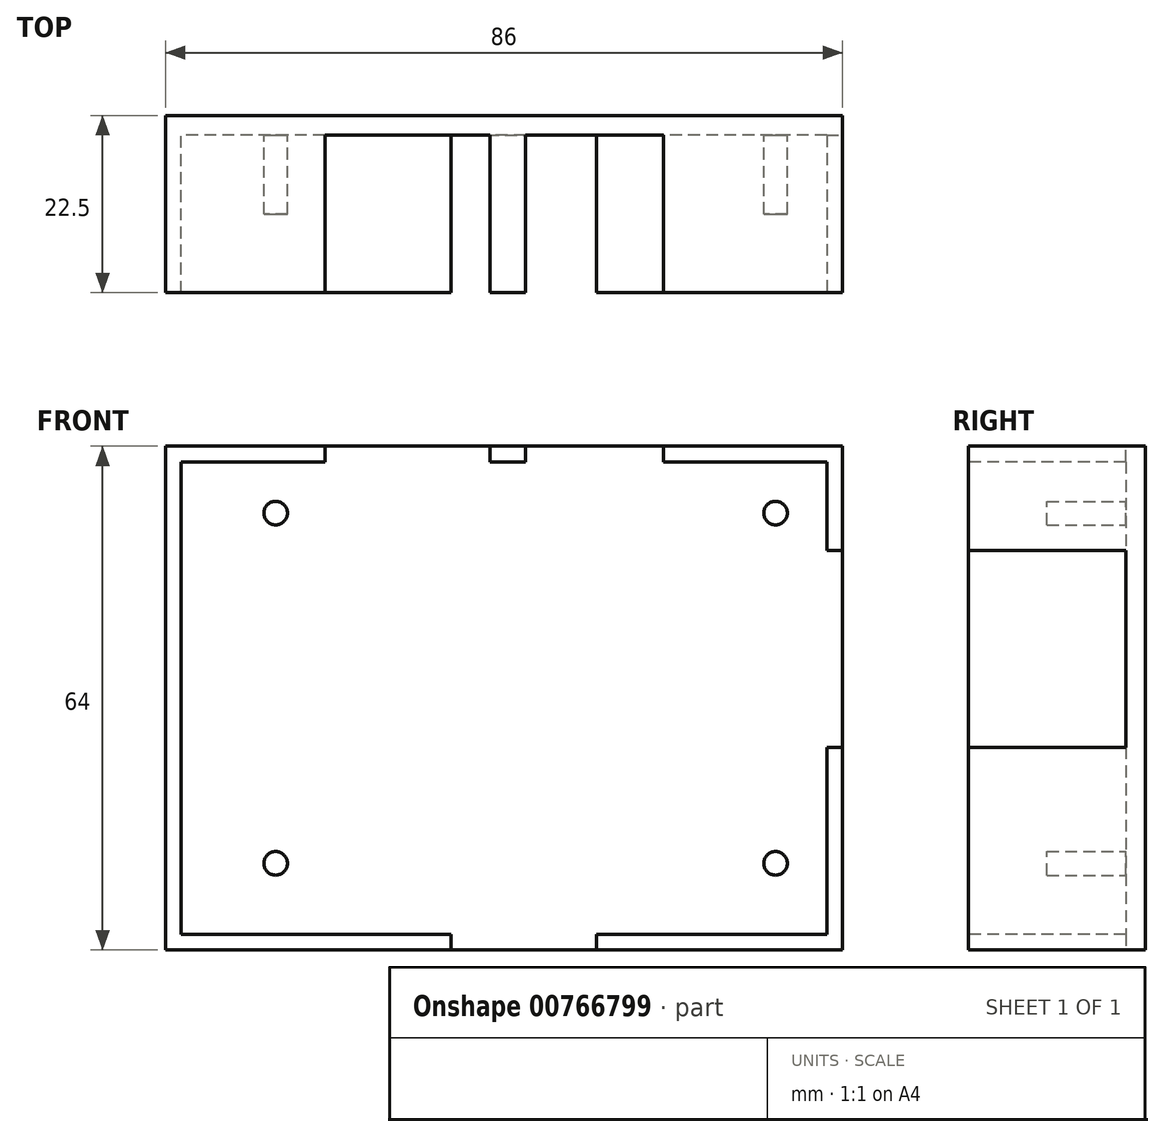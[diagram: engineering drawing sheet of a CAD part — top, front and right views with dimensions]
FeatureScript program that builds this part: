
annotation { "Feature Type Name" : "Feature", "Feature Type Description" : "" }
export const myFeature = defineFeature(function(context is Context, id is Id, definition is map)
    precondition{}
    {
        {
            var Q0;
            Q0=qCreatedBy(makeId("Front.planeOp"),FACE);
            var sketch = newSketch(context, id + "F0", { "sketchPlane" : qUnion([Q0])});
            skLineSegment(sketch, "E0.bottom", {"start": v(41, 30) * mm, "end": v(-41, 30) * mm});
            skLineSegment(sketch, "E0.top", {"start": v(41, -30) * mm, "end": v(-41, -30) * mm});
            skLineSegment(sketch, "E0.left", {"start": v(41, 30) * mm, "end": v(41, -30) * mm});
            skLineSegment(sketch, "E0.right", {"start": v(-41, 30) * mm, "end": v(-41, -30) * mm});
            skPoint(sketch, "E0.middle", {"position": v(0, 0) * mm});
            skCircle(sketch, "E1", {"center": v(-29, -21) * mm, "radius": 1.5 * mm});
            skCircle(sketch, "E2", {"center": v(-29, 23.5) * mm, "radius": 1.5 * mm});
            skCircle(sketch, "E3", {"center": v(34.5, 23.5) * mm, "radius": 1.5 * mm});
            skCircle(sketch, "E4", {"center": v(34.5, -21) * mm, "radius": 1.5 * mm});
            skLineSegment(sketch, "E5.bottom", {"start": v(43, 32) * mm, "end": v(-43, 32) * mm});
            skLineSegment(sketch, "E5.top", {"start": v(43, -32) * mm, "end": v(-43, -32) * mm});
            skLineSegment(sketch, "E5.left", {"start": v(43, 32) * mm, "end": v(43, -32) * mm});
            skLineSegment(sketch, "E5.right", {"start": v(-43, 32) * mm, "end": v(-43, -32) * mm});
            skSolve(sketch);
        }
        {
            var Q0;
            Q0=makeQuery(id+"F0.imprint","IMPRINT",FACE,{"disambiguationData":[TD([[makeQuery(id+"F0.imprint","IMPRINT",EDGE,{"derivedFrom":sQuery(id+"F0.wireOp",EDGE,"E0.bottom")}),-1.0]])]});
            var Q1;
            Q1=makeQuery(id+"F0.imprint","IMPRINT",FACE,{"disambiguationData":[TD([[makeQuery(id+"F0.imprint","IMPRINT",EDGE,{"derivedFrom":sQuery(id+"F0.wireOp",EDGE,"E2")}),1.0]])]});
            var Q2;
            Q2=makeQuery(id+"F0.imprint","IMPRINT",FACE,{"disambiguationData":[TD([[makeQuery(id+"F0.imprint","IMPRINT",EDGE,{"derivedFrom":sQuery(id+"F0.wireOp",EDGE,"E0.bottom")}),1.0]])]});
            var Q3;
            Q3=makeQuery(id+"F0.imprint","IMPRINT",FACE,{"disambiguationData":[TD([[makeQuery(id+"F0.imprint","IMPRINT",EDGE,{"derivedFrom":sQuery(id+"F0.wireOp",EDGE,"E1")}),1.0]])]});
            var Q4;
            Q4=makeQuery(id+"F0.imprint","IMPRINT",FACE,{"disambiguationData":[TD([[makeQuery(id+"F0.imprint","IMPRINT",EDGE,{"derivedFrom":sQuery(id+"F0.wireOp",EDGE,"E4")}),1.0]])]});
            var Q5;
            Q5=makeQuery(id+"F0.imprint","IMPRINT",FACE,{"disambiguationData":[TD([[makeQuery(id+"F0.imprint","IMPRINT",EDGE,{"derivedFrom":sQuery(id+"F0.wireOp",EDGE,"E3")}),1.0]])]});
            extrude(context, id + "F1", {"entities" : qUnion([Q0, Q1, Q2, Q3, Q4, Q5]), "oppositeDirection" : true, "depth" : 2.5 * mm, "offsetDistance" : 25 * mm});
        }
        {
            var Q0;
            Q0=makeQuery(id+"F0.imprint","IMPRINT",FACE,{"disambiguationData":[TD([[makeQuery(id+"F0.imprint","IMPRINT",EDGE,{"derivedFrom":sQuery(id+"F0.wireOp",EDGE,"E2")}),1.0]])]});
            var Q1;
            Q1=makeQuery(id+"F0.imprint","IMPRINT",FACE,{"disambiguationData":[TD([[makeQuery(id+"F0.imprint","IMPRINT",EDGE,{"derivedFrom":sQuery(id+"F0.wireOp",EDGE,"E1")}),1.0]])]});
            var Q2;
            Q2=makeQuery(id+"F0.imprint","IMPRINT",FACE,{"disambiguationData":[TD([[makeQuery(id+"F0.imprint","IMPRINT",EDGE,{"derivedFrom":sQuery(id+"F0.wireOp",EDGE,"E4")}),1.0]])]});
            var Q3;
            Q3=makeQuery(id+"F0.imprint","IMPRINT",FACE,{"disambiguationData":[TD([[makeQuery(id+"F0.imprint","IMPRINT",EDGE,{"derivedFrom":sQuery(id+"F0.wireOp",EDGE,"E3")}),1.0]])]});
            extrude(context, id + "F2", {"entities" : qUnion([Q0, Q1, Q2, Q3]), "operationType" : NewBodyOperationType.ADD, "depth" : 10 * mm, "offsetDistance" : 25 * mm});
        }
        {
            var Q0;
            Q0=makeQuery(id+"F0.imprint","IMPRINT",FACE,{"disambiguationData":[TD([[makeQuery(id+"F0.imprint","IMPRINT",EDGE,{"derivedFrom":sQuery(id+"F0.wireOp",EDGE,"E0.bottom")}),-1.0]])]});
            extrude(context, id + "F3", {"entities" : qUnion([Q0]), "operationType" : NewBodyOperationType.ADD, "depth" : 20 * mm, "offsetDistance" : 25 * mm});
        }
        {
            var Q0;
            {var subQ0=sQuery(id+"F0.wireOp",EDGE,"E5.left");Q0=makeQuery(id+"F3.boolean.opBoolean","MERGE",FACE,{"derivedFrom":[makeQuery(id+"F1.opExtrude","SWEPT_FACE",FACE,{"disambiguationData":[OSD([subQ0])]}),makeQuery(id+"F3.opExtrude","SWEPT_FACE",FACE,{"disambiguationData":[OSD([subQ0])]})]});}
            var sketch = newSketch(context, id + "F4", { "sketchPlane" : qUnion([Q0])});
            skLineSegment(sketch, "E6.bottom", {"start": v(0, 18.75) * mm, "end": v(-20, 18.75) * mm});
            skLineSegment(sketch, "E6.top", {"start": v(0, -6.25) * mm, "end": v(-20, -6.25) * mm});
            skLineSegment(sketch, "E6.left", {"start": v(0, 18.75) * mm, "end": v(0, -6.25) * mm});
            skLineSegment(sketch, "E6.right", {"start": v(-20, 18.75) * mm, "end": v(-20, -6.25) * mm});
            skSolve(sketch);
        }
        {
            var Q0;
            Q0 = qSketchRegion(id + "F4", true);
            extrude(context, id + "F5", {"entities" : qUnion([Q0]), "operationType" : NewBodyOperationType.REMOVE, "oppositeDirection" : true, "depth" : 2 * mm, "offsetDistance" : 25 * mm});
        }
        {
            var Q0;
            {var subQ0=sQuery(id+"F0.wireOp",EDGE,"E5.top");Q0=makeQuery(id+"F3.boolean.opBoolean","MERGE",FACE,{"derivedFrom":[makeQuery(id+"F1.opExtrude","SWEPT_FACE",FACE,{"disambiguationData":[OSD([subQ0])]}),makeQuery(id+"F3.opExtrude","SWEPT_FACE",FACE,{"disambiguationData":[OSD([subQ0])]})]});}
            var sketch = newSketch(context, id + "F6", { "sketchPlane" : qUnion([Q0])});
            skLineSegment(sketch, "E7.bottom", {"start": v(-6.75, 0) * mm, "end": v(11.75, 0) * mm});
            skLineSegment(sketch, "E7.top", {"start": v(-6.75, 20) * mm, "end": v(11.75, 20) * mm});
            skLineSegment(sketch, "E7.left", {"start": v(-6.75, 0) * mm, "end": v(-6.75, 20) * mm});
            skLineSegment(sketch, "E7.right", {"start": v(11.75, 0) * mm, "end": v(11.75, 20) * mm});
            skSolve(sketch);
        }
        {
            var Q0;
            Q0 = qSketchRegion(id + "F6", true);
            extrude(context, id + "F7", {"entities" : qUnion([Q0]), "operationType" : NewBodyOperationType.REMOVE, "oppositeDirection" : true, "depth" : 2 * mm, "offsetDistance" : 25 * mm});
        }
        {
            var Q0;
            {var subQ0=sQuery(id+"F0.wireOp",EDGE,"E5.bottom");Q0=makeQuery(id+"F3.boolean.opBoolean","MERGE",FACE,{"derivedFrom":[makeQuery(id+"F1.opExtrude","SWEPT_FACE",FACE,{"disambiguationData":[OSD([subQ0])]}),makeQuery(id+"F3.opExtrude","SWEPT_FACE",FACE,{"disambiguationData":[OSD([subQ0])]})]});}
            var sketch = newSketch(context, id + "F8", { "sketchPlane" : qUnion([Q0])});
            skLineSegment(sketch, "E8.bottom", {"start": v(-22.75, 0) * mm, "end": v(-1.75, 0) * mm});
            skLineSegment(sketch, "E8.top", {"start": v(-22.75, -20) * mm, "end": v(-1.75, -20) * mm});
            skLineSegment(sketch, "E8.left", {"start": v(-22.75, 0) * mm, "end": v(-22.75, -20) * mm});
            skLineSegment(sketch, "E8.right", {"start": v(-1.75, 0) * mm, "end": v(-1.75, -20) * mm});
            skLineSegment(sketch, "E9.bottom", {"start": v(2.75, 0) * mm, "end": v(20.25, 0) * mm});
            skLineSegment(sketch, "E9.top", {"start": v(2.75, -20) * mm, "end": v(20.25, -20) * mm});
            skLineSegment(sketch, "E9.left", {"start": v(2.75, 0) * mm, "end": v(2.75, -20) * mm});
            skLineSegment(sketch, "E9.right", {"start": v(20.25, 0) * mm, "end": v(20.25, -20) * mm});
            skSolve(sketch);
        }
        {
            var Q0;
            Q0 = qSketchRegion(id + "F8", true);
            extrude(context, id + "F9", {"entities" : qUnion([Q0]), "operationType" : NewBodyOperationType.REMOVE, "oppositeDirection" : true, "depth" : 2 * mm, "offsetDistance" : 25 * mm});
        }
    });
